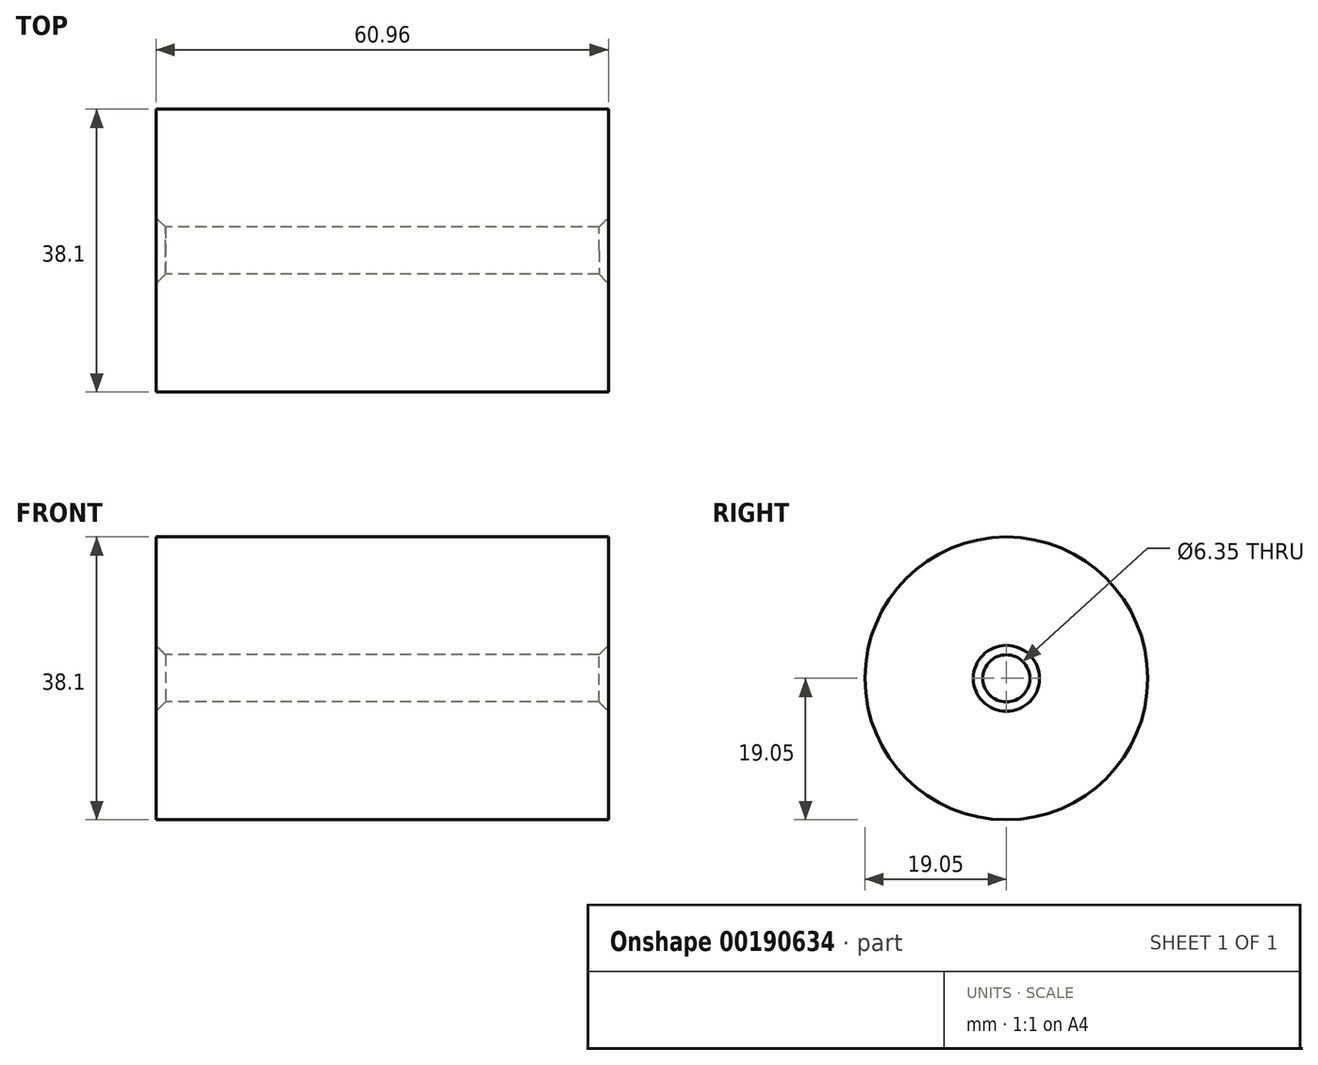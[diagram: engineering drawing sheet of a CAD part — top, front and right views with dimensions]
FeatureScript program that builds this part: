
annotation { "Feature Type Name" : "Feature", "Feature Type Description" : "" }
export const myFeature = defineFeature(function(context is Context, id is Id, definition is map)
    precondition{}
    {
        {
            var Q0;
            Q0=qCreatedBy(makeId("Right.planeOp"),FACE);
            var sketch = newSketch(context, id + "F0", { "sketchPlane" : qUnion([Q0])});
            skCircle(sketch, "E0", {"center": v(0, 0) * mm, "radius": 19.05 * mm});
            skCircle(sketch, "E1", {"center": v(0, 0) * mm, "radius": 3.18 * mm});
            skSolve(sketch);
        }
        {
            var Q0;
            Q0 = qSketchRegion(id + "F0", true);
            extrude(context, id + "F1", {"entities" : qUnion([Q0]), "depth" : 30.48 * mm});
        }
        {
            var Q0;
            Q0=makeQuery(id+"F1.opExtrude","SWEPT_BODY",BODY,{"disambiguationData":[OSD([sQuery(id+"F0.wireOp",EDGE,"E0")])]});
            var Q1;
            Q1=makeQuery(id+"F1.opExtrude","CAP_FACE",FACE,{"disambiguationData":[OSD([sQuery(id+"F0.wireOp",EDGE,"E0")])],"isStart":true});
            mirror(context, id + "F2", {"operationType" : NewBodyOperationType.ADD, "entities" : qUnion([Q0]), "mirrorPlane" : qUnion([Q1])});
        }
        {
            var Q0;
            Q0=makeQuery(id+"F1.opExtrude","CAP_EDGE",EDGE,{"disambiguationData":[OSD([sQuery(id+"F0.wireOp",EDGE,"E1")])],"isStart":false});
            var Q1;
            Q1=makeQuery(id+"F2.opPattern","COPY",EDGE,{"derivedFrom":makeQuery(id+"F1.opExtrude","CAP_EDGE",EDGE,{"disambiguationData":[OSD([sQuery(id+"F0.wireOp",EDGE,"E1")])],"isStart":false}),"instanceName":"1"});
            chamfer(context, id + "F3", {"entities" : qUnion([Q0, Q1]), "width" : 1.27 * mm, "tangentPropagation" : true});
        }
    });
